# Revit family: EKF_EE_КорпусДвухдверныйFORT_IP54_PROxima
name_source: partatom
category: Электрооборудование
units: mm (PartAtom-declared; Revit-internal decimal feet)

## family parameters
Всегда вертикально = Нет
На основе рабочей плоскости = Да
Общий = Да
При загрузке вырезать с полостями = Нет
Размер круглого соединителя = Использовать диаметр
Тип детали = Силовой щит
Точка расчета площади = Нет

## types (9) — shared parameters
ADSK_Единица измерения = шт.
ADSK_Завод-изготовитель = EKF
ADSK_Количество = 1
ADSK_Марка = Корпус FORT
ADSK_Материал = RAL 7035_Сталь
ADSK_Обозначение = Корпус FORT
ADSK_Размер_Ширина = 1000 мм
D = 10 мм
Дверь_t = 21 мм
Дверь_Ширина = 498 мм
ЗадняяПанель_t = 24 мм
Изготовитель = EKF
КолОтв = 4
Крышка_t = 14 мм
Отступ = 20 мм
Серия номенклатуры = PROxima
Степень защиты IP = IP54
ТВ = EKF_2
Тип установки = Напольный
zero-valued in all types: ADSK_Масса, Отметка по умолчанию

## per-type parameters (varying)
| type | ADSK_Код изделия | ADSK_Размер_Высота | ADSK_Размер_Глубина | Каркас_h | Каркас_Глубина | Тип |
| Корпус FORT IP54 (1800x1000x400) EKF PROxima | FK18104G | 1800 мм | 400 мм | 1786 мм | 350.5 мм | 216 мм |
| Корпус FORT IP54 (1800x1000x600) EKF PROxima | FK18106G | 1800 мм | 600 мм | 1786 мм | 550.5 мм | 217 мм |
| Корпус FORT IP54 (1800x1000x800) EKF PROxima | FK18108G | 1800 мм | 800 мм | 1786 мм | 750.5 мм | 218 мм |
| Корпус FORT IP54 (2000x1000x400) EKF PROxima | FK20104G | 2000 мм | 400 мм | 1986 мм | 350.5 мм | 225 мм |
| Корпус FORT IP54 (2000x1000x600) EKF PROxima | FK20106G | 2000 мм | 600 мм | 1986 мм | 550.5 мм | 226 мм |
| Корпус FORT IP54 (2000x1000x800) EKF PROxima | FK20108G | 2000 мм | 800 мм | 1986 мм | 750.5 мм | 227 мм |
| Корпус FORT IP54 (2200x1000x400) EKF PROxima | FK22104G | 2200 мм | 400 мм | 2186 мм | 350.5 мм | 237 мм |
| Корпус FORT IP54 (2200x1000x600) EKF PROxima | FK22106G | 2200 мм | 600 мм | 2186 мм | 550.5 мм | 238 мм |
| Корпус FORT IP54 (2200x1000x800) EKF PROxima | FK22108G | 2200 мм | 800 мм | 2186 мм | 750.5 мм | 239 мм |

note: column(s) folded — value = type name in every type: ADSK_Наименование
